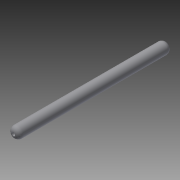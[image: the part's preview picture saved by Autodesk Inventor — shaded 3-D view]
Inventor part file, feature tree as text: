
AUTODESK INVENTOR PART (.ipt)
format: ipt  version: 2013 (Build 170138000, 138)  size: 81,920 bytes
history: native  units: in
note: dims shown in document units (in); Inventor stores cm internally (conversion verified against a paired STEP export)
features: extrude x1, fillet x1, sketch x1
ambient origin geometry x8: Origin, YZ Plane, XZ Plane, XY Plane, X Axis, Y Axis, Z Axis, Center Point
bodies: Solid1 (feature_tree)
feature tree (3):
  extrude  "Extrusion1"  Depth=0.75in
  fillet  "Fillet1"  Radius=33.75in
  sketch  "Sketch1"  dims[d0=2.5in d1=0.75in d2=33.75in d3=0.0in d4=1.0in]
